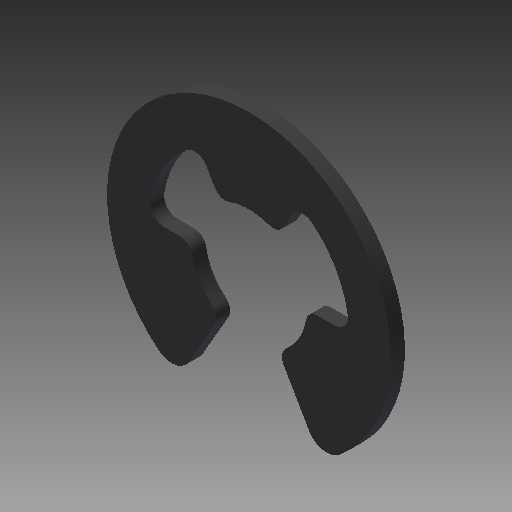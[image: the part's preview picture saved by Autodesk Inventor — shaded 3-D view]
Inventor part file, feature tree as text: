
AUTODESK INVENTOR PART (.ipt)
format: ipt  version: 2019.4 (Build 234330000, 330)  size: 137,216 bytes
history: native  units: in
note: dims shown in document units (in); Inventor stores cm internally (conversion verified against a paired STEP export)
features: other x7, extrude x1, sketch x1
ambient origin geometry x8: Origin, YZ Plane, XZ Plane, XY Plane, X Axis, Y Axis, Z Axis, Center Point
bodies: Solid1 (feature_tree)
feature tree (9):
  extrude  "Extrusion1"  [1 undecoded]
  other  "RR_XY"
  other  "RR_YZ"
  other  "RR_ZX"
  other  "RR_X"
  other  "RR_Y"
  other  "RR_Z"
  other  "RR_Center"
  sketch  "Sketch_1"  dims[d0=0.0365in d1=0.0in]
note: 1 required parameter value undecoded (feature->parameter linkage not recoverable at this tier; creation-order binding heuristic only, values carry confidence <= 0.55)
